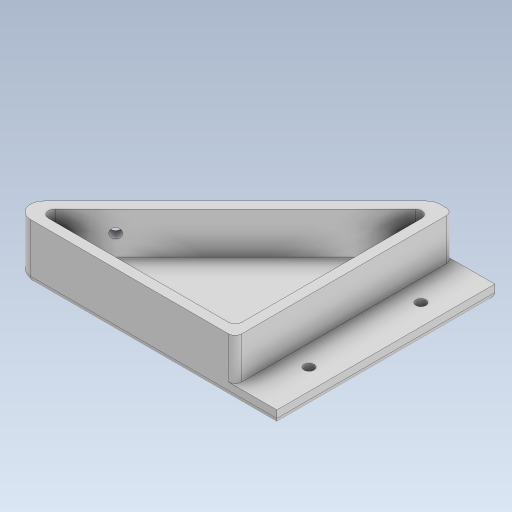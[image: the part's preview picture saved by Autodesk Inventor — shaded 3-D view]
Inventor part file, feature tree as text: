
AUTODESK INVENTOR PART (.ipt)
format: ipt  version: 2023 (Build 270158000, 158)  size: 381,952 bytes
history: native  units: in
note: dims shown in document units (in); Inventor stores cm internally (conversion verified against a paired STEP export)
features: extrude x4, sketch x4, fillet x1, projected_geometry x1
ambient origin geometry x8: Origin, YZ Plane, XZ Plane, XY Plane, X Axis, Y Axis, Z Axis, Center Point
bodies: Solid1 (feature_tree)
feature tree (10):
  extrude  "Extrusion1"  Depth=0.25in
  extrude  "Extrusion2"  Depth=0.7874in TaperAngle=0.0deg
  extrude  "Extrusion3"  Depth=0.7874in
  extrude  "Extrusion4"  Depth=0.7874in
  fillet  "Fillet1"  Radius=1.0in
  sketch  "Sketch1"  dims[d0=4.4643in d1=0.25in]
  sketch  "Sketch2"  dims[d2=0.2635in d3=0.0in d5=0.7874in d6=0.0in]
  projected_geometry  "Projected Loop1"
  sketch  "Sketch3"  dims[d7=0.125in d8=0.7874in]
  sketch  "Sketch5"  dims[d9=0.3937in d10=1.0in d11=1.0in d12=0.1905in d13=0.51in d14=0.0in d15=4.5in d17=0.6572in d18=0.2635in d19=0.1875in d20=0.7874in d21=0.0in]
